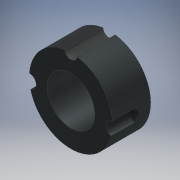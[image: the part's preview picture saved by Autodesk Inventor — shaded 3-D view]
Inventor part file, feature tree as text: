
AUTODESK INVENTOR PART (.ipt)
format: ipt  version: 2018 (Build 220112000, 112)  size: 152,576 bytes
history: native  units: mm
features: sketch x7, extrude x5, hole x2, other x1
ambient origin geometry x8: Origin, YZ Plane, XZ Plane, XY Plane, X Axis, Y Axis, Z Axis, Center Point
bodies: Solido1 (feature_tree)
feature tree (15):
  extrude  "Estrusione1"  Depth=30.0mm
  extrude  "Estrusione2"  Depth=80.0mm
  hole  "Foro1"  [1 undecoded]
  hole  "Foro2"  [1 undecoded]
  extrude  "Estrusione3"  Depth=34.0mm TaperAngle=0.0deg
  extrude  "Estrusione4"  Depth=69.77mm
  extrude  "Estrusione5"  Depth=16.580628mm
  sketch  "Schizzo1"
  sketch  "Schizzo2"
  sketch  "Schizzo3"
  sketch  "Schizzo4"
  sketch  "Schizzo5"
  sketch  "Schizzo6"
  other  "Linea chiusa proiettata1"
  sketch  "Schizzo7"
note: 2 required parameter values undecoded (feature->parameter linkage not recoverable at this tier; creation-order binding heuristic only, values carry confidence <= 0.55)
